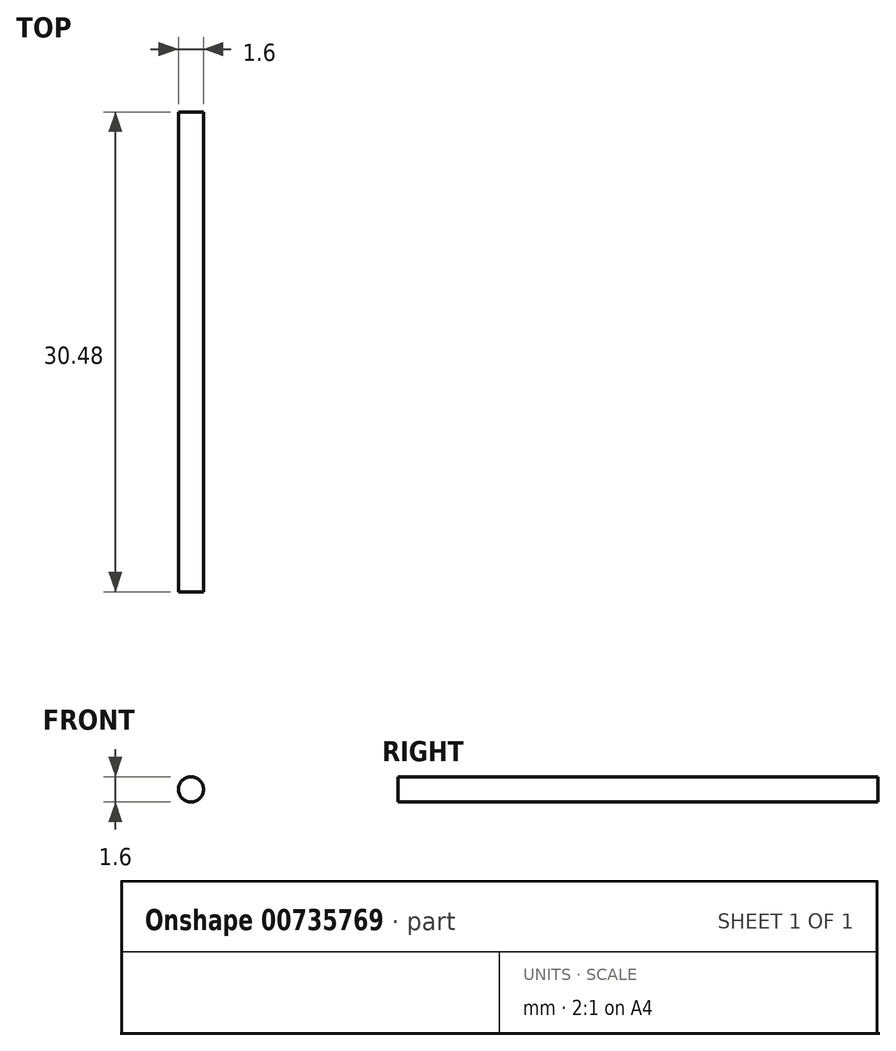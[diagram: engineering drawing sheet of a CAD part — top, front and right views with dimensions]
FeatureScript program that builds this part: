
annotation { "Feature Type Name" : "Feature", "Feature Type Description" : "" }
export const myFeature = defineFeature(function(context is Context, id is Id, definition is map)
    precondition{}
    {
        {
            var Q0;
            Q0=qCreatedBy(makeId("Front.planeOp"),FACE);
            var sketch = newSketch(context, id + "F0", { "sketchPlane" : qUnion([Q0])});
            skCircle(sketch, "E0", {"center": v(0, 0) * mm, "radius": 0.8 * mm});
            skSolve(sketch);
        }
        {
            var Q0;
            Q0=makeQuery(id+"F0.imprint","IMPRINT",FACE,{"disambiguationData":[TD([[makeQuery(id+"F0.imprint","IMPRINT",EDGE,{"derivedFrom":sQuery(id+"F0.wireOp",EDGE,"E0")}),1.0]])]});
            extrude(context, id + "F1", {"entities" : qUnion([Q0]), "depth" : 30.48 * mm, "offsetDistance" : 25.4 * mm});
        }
    });
